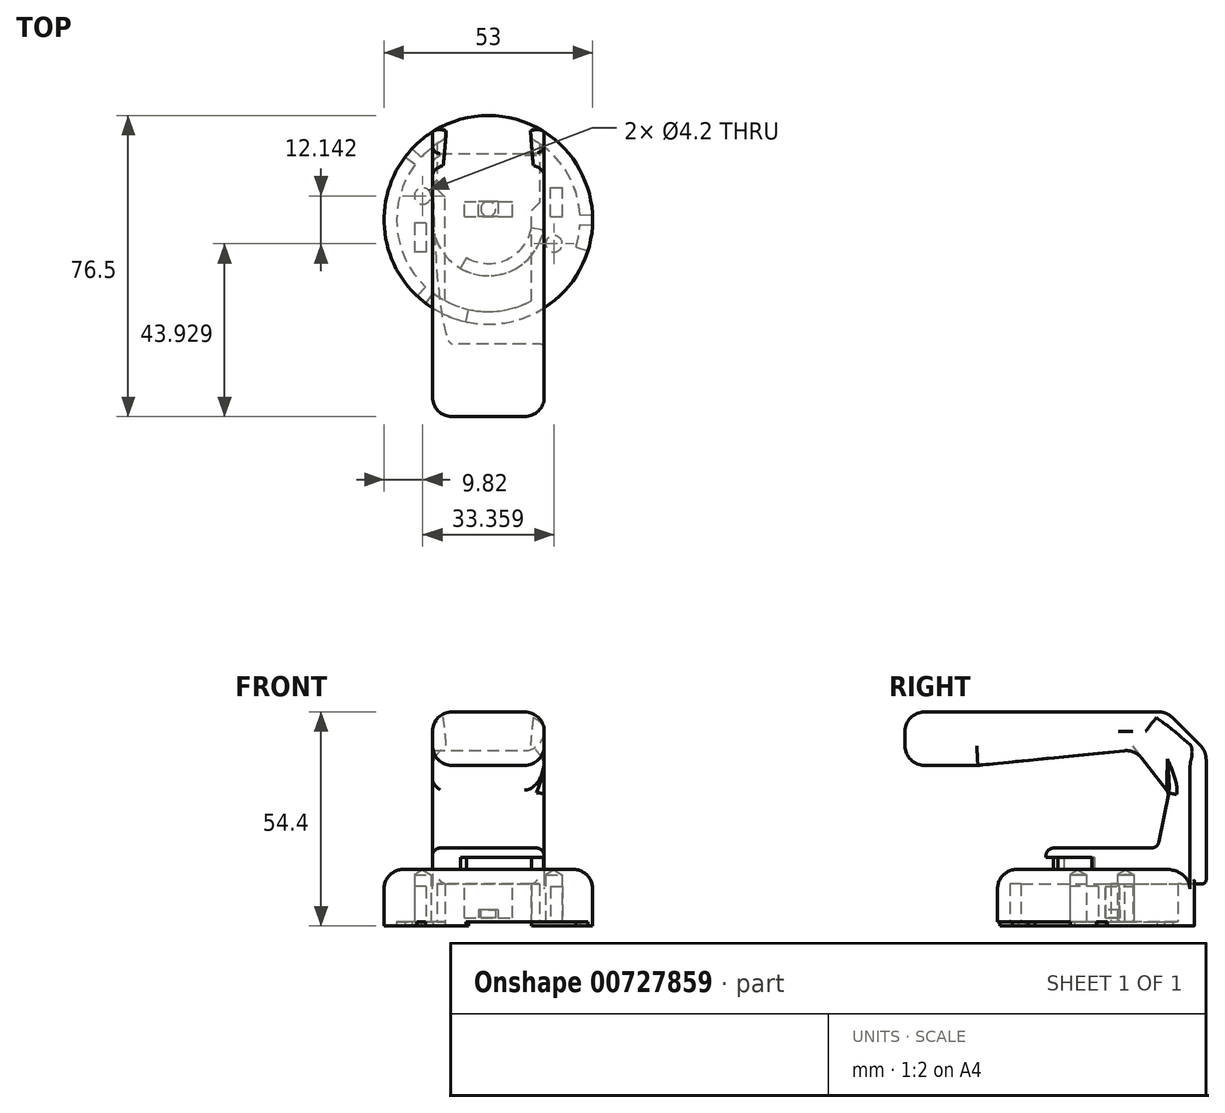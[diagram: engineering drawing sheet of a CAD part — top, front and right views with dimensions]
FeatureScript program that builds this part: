
annotation { "Feature Type Name" : "Feature", "Feature Type Description" : "" }
export const myFeature = defineFeature(function(context is Context, id is Id, definition is map)
    precondition{}
    {
        {
            var Q0;
            Q0=qCreatedBy(makeId("Top.planeOp"),FACE);
            var sketch = newSketch(context, id + "F0", { "sketchPlane" : qUnion([Q0])});
            skCircle(sketch, "E0", {"center": v(0, 0) * mm, "radius": 26.5 * mm});
            skSolve(sketch);
        }
        {
            var Q0;
            Q0=makeQuery(id+"F0.imprint","IMPRINT",FACE,{"disambiguationData":[TD([[makeQuery(id+"F0.imprint","IMPRINT",EDGE,{"derivedFrom":sQuery(id+"F0.wireOp",EDGE,"E0")}),1.0]])]});
            extrude(context, id + "F1", {"entities" : qUnion([Q0]), "depth" : 14.4 * mm, "offsetDistance" : 25 * mm});
        }
        {
            var Q0;
            Q0=makeQuery(id+"F1.opExtrude","CAP_FACE",FACE,{"disambiguationData":[OSD([sQuery(id+"F0.wireOp",EDGE,"E0")])],"isStart":false});
            var sketch = newSketch(context, id + "F2", { "sketchPlane" : qUnion([Q0])});
            skCircle(sketch, "E1", {"center": v(0, 0) * mm, "radius": 14.2 * mm});
            skSolve(sketch);
        }
        {
            var Q0;
            Q0 = qSketchRegion(id + "F2", true);
            extrude(context, id + "F3", {"entities" : qUnion([Q0]), "depth" : 5.4 * mm, "offsetDistance" : 25 * mm});
        }
        {
            var Q0;
            Q0=makeQuery(id+"F1.opExtrude","CAP_FACE",FACE,{"disambiguationData":[OSD([sQuery(id+"F0.wireOp",EDGE,"E0")])],"isStart":false});
            var sketch = newSketch(context, id + "F4", { "sketchPlane" : qUnion([Q0])});
            skLineSegment(sketch, "E2", {"start": v(0, 0) * mm, "end": v(-7.1, -12.3) * mm});
            skLineSegment(sketch, "E3", {"start": v(0, 0) * mm, "end": v(13.98, -2.47) * mm});
            skArc(sketch, "E4", {"start": v(13.98, -2.47) * mm, "mid": v(6, -12.87) * mm, "end": v(-7.1, -12.3) * mm});
            skSolve(sketch);
        }
        {
            var Q0;
            Q0 = qSketchRegion(id + "F4", true);
            extrude(context, id + "F5", {"entities" : qUnion([Q0]), "operationType" : NewBodyOperationType.REMOVE, "depth" : 3 * mm, "offsetDistance" : 25 * mm});
        }
        {
            var Q0;
            Q0=makeQuery(id+"F1.opExtrude","CAP_FACE",FACE,{"disambiguationData":[OSD([sQuery(id+"F0.wireOp",EDGE,"E0")])],"isStart":false});
            var sketch = newSketch(context, id + "F6", { "sketchPlane" : qUnion([Q0])});
            skCircle(sketch, "E5", {"center": v(0, 0) * mm, "radius": 11.1 * mm});
            skSolve(sketch);
        }
        {
            var Q0;
            Q0 = qSketchRegion(id + "F6", true);
            var Q1;
            Q1=makeQuery(id+"F5.boolean.opBoolean","COPY",FACE,{"derivedFrom":makeQuery(id+"F5.opExtrude","CAP_FACE",FACE,{"disambiguationData":[OSD([sQuery(id+"F4.wireOp",EDGE,"E2"),sQuery(id+"F4.wireOp",EDGE,"E3"),sQuery(id+"F4.wireOp",EDGE,"E4")])],"isStart":false})});
            extrude(context, id + "F7", {"entities" : qUnion([Q0]), "endBound" : BoundingType.UP_TO_SURFACE, "depth" : 25 * mm, "endBoundEntityFace" : qUnion([Q1]), "offsetDistance" : 25 * mm});
        }
        {
            var Q0;
            Q0=makeQuery(id+"F1.opExtrude","CAP_FACE",FACE,{"disambiguationData":[OSD([sQuery(id+"F0.wireOp",EDGE,"E0")])],"isStart":true});
            var sketch = newSketch(context, id + "F8", { "sketchPlane" : qUnion([Q0])});
            skCircle(sketch, "E6", {"center": v(0, 0) * mm, "radius": 23.3 * mm});
            skSolve(sketch);
        }
        {
            var Q0;
            Q0 = qSketchRegion(id + "F8", true);
            extrude(context, id + "F9", {"entities" : qUnion([Q0]), "operationType" : NewBodyOperationType.REMOVE, "oppositeDirection" : true, "depth" : 1 * mm, "offsetDistance" : 25 * mm});
        }
        {
            var Q0;
            Q0=makeQuery(id+"F8.imprint","IMPRINT",FACE,{"disambiguationData":[TD([[makeQuery(id+"F8.imprint","IMPRINT",EDGE,{"derivedFrom":sQuery(id+"F8.wireOp",EDGE,"E6")}),-1.0]])]});
            var sketch = newSketch(context, id + "F10", { "sketchPlane" : qUnion([Q0])});
            skLineSegment(sketch, "E7.top", {"start": v(-11, -26.5) * mm, "end": v(11, -26.5) * mm});
            skLineSegment(sketch, "E7.left", {"start": v(-11, 20.54) * mm, "end": v(-11, -26.5) * mm});
            skLineSegment(sketch, "E7.right", {"start": v(11, 20.54) * mm, "end": v(11, -26.5) * mm});
            skArc(sketch, "E8", {"start": v(-11, 20.54) * mm, "mid": v(0, 23.3) * mm, "end": v(11, 20.54) * mm});
            skSolve(sketch);
        }
        {
            var Q0;
            Q0 = qSketchRegion(id + "F10", true);
            extrude(context, id + "F11", {"entities" : qUnion([Q0]), "operationType" : NewBodyOperationType.REMOVE, "oppositeDirection" : true, "depth" : 10.7 * mm, "offsetDistance" : 25 * mm});
        }
        {
            var Q0;
            Q0=makeQuery(id+"F8.imprint","IMPRINT",FACE,{"disambiguationData":[TD([[makeQuery(id+"F8.imprint","IMPRINT",EDGE,{"derivedFrom":sQuery(id+"F8.wireOp",EDGE,"E6")}),-1.0]])]});
            var sketch = newSketch(context, id + "F12", { "sketchPlane" : qUnion([Q0])});
            skLineSegment(sketch, "E9.top", {"start": v(13, -4.34) * mm, "end": v(0, -4.34) * mm});
            skLineSegment(sketch, "E9.left", {"start": v(13, -19.34) * mm, "end": v(13, -4.34) * mm});
            skLineSegment(sketch, "E9.right", {"start": v(0, -23.3) * mm, "end": v(0, -4.34) * mm});
            skArc(sketch, "E10", {"start": v(13, -19.34) * mm, "mid": v(6.8, -22.29) * mm, "end": v(0, -23.3) * mm});
            skSolve(sketch);
        }
        {
            var Q0;
            Q0 = qSketchRegion(id + "F12", true);
            var Q1;
            Q1=makeQuery(id+"F11.boolean.opBoolean","COPY",FACE,{"derivedFrom":makeQuery(id+"F11.opExtrude","CAP_FACE",FACE,{"disambiguationData":[OSD([sQuery(id+"F10.wireOp",EDGE,"E7.top"),sQuery(id+"F10.wireOp",EDGE,"E7.left"),sQuery(id+"F10.wireOp",EDGE,"E7.right"),sQuery(id+"F10.wireOp",EDGE,"E8")])],"isStart":false})});
            extrude(context, id + "F13", {"entities" : qUnion([Q0]), "operationType" : NewBodyOperationType.REMOVE, "endBound" : BoundingType.UP_TO_SURFACE, "oppositeDirection" : true, "depth" : 10.7 * mm, "endBoundEntityFace" : qUnion([Q1]), "offsetDistance" : 25 * mm});
        }
        {
            var Q0;
            Q0=makeQuery(id+"F13.boolean.opBoolean","INTERSECT",EDGE,{"derivedFrom":[makeQuery(id+"F11.boolean.opBoolean","COPY",FACE,{"derivedFrom":makeQuery(id+"F11.opExtrude","SWEPT_FACE",FACE,{"disambiguationData":[OSD([sQuery(id+"F10.wireOp",EDGE,"E7.right")])]})}),makeQuery(id+"F13.opExtrude","SWEPT_FACE",FACE,{"disambiguationData":[OSD([sQuery(id+"F12.wireOp",EDGE,"E9.top")])]})]});
            chamfer(context, id + "F14", {"entities" : qUnion([Q0]), "width" : 2 * mm, "tangentPropagation" : true});
        }
        {
            var Q0;
            Q0=makeQuery(id+"F8.imprint","IMPRINT",FACE,{"disambiguationData":[TD([[makeQuery(id+"F8.imprint","IMPRINT",EDGE,{"derivedFrom":sQuery(id+"F8.wireOp",EDGE,"E6")}),-1.0]])]});
            var sketch = newSketch(context, id + "F15", { "sketchPlane" : qUnion([Q0])});
            skLineSegment(sketch, "E11.top", {"start": v(-13, -7.84) * mm, "end": v(0, -7.84) * mm});
            skLineSegment(sketch, "E11.left", {"start": v(-13, -19.34) * mm, "end": v(-13, -7.84) * mm});
            skLineSegment(sketch, "E11.right", {"start": v(0, -23.3) * mm, "end": v(0, -7.84) * mm});
            skArc(sketch, "E12", {"start": v(-13, -19.34) * mm, "mid": v(-6.8, -22.29) * mm, "end": v(0, -23.3) * mm});
            skSolve(sketch);
        }
        {
            var Q0;
            Q0 = qSketchRegion(id + "F15", true);
            var Q1;
            Q1=makeQuery(id+"F13.boolean.opBoolean","MERGE",FACE,{"derivedFrom":[makeQuery(id+"F11.boolean.opBoolean","COPY",FACE,{"derivedFrom":makeQuery(id+"F11.opExtrude","CAP_FACE",FACE,{"disambiguationData":[OSD([sQuery(id+"F10.wireOp",EDGE,"E7.top"),sQuery(id+"F10.wireOp",EDGE,"E7.left"),sQuery(id+"F10.wireOp",EDGE,"E7.right"),sQuery(id+"F10.wireOp",EDGE,"E8")])],"isStart":false})})],"fromTools":[makeQuery(id+"F13.opExtrude","CAP_FACE",FACE,{"disambiguationData":[OSD([sQuery(id+"F12.wireOp",EDGE,"E9.top"),sQuery(id+"F12.wireOp",EDGE,"E9.left"),sQuery(id+"F12.wireOp",EDGE,"E9.right"),sQuery(id+"F12.wireOp",EDGE,"E10")])],"isStart":false})]});
            extrude(context, id + "F16", {"entities" : qUnion([Q0]), "operationType" : NewBodyOperationType.REMOVE, "endBound" : BoundingType.UP_TO_SURFACE, "oppositeDirection" : true, "depth" : 25 * mm, "endBoundEntityFace" : qUnion([Q1]), "offsetDistance" : 25 * mm});
        }
        {
            var Q0;
            Q0=makeQuery(id+"F16.boolean.opBoolean","INTERSECT",EDGE,{"derivedFrom":[makeQuery(id+"F11.boolean.opBoolean","COPY",FACE,{"derivedFrom":makeQuery(id+"F11.opExtrude","SWEPT_FACE",FACE,{"disambiguationData":[OSD([sQuery(id+"F10.wireOp",EDGE,"E7.left")])]})}),makeQuery(id+"F16.opExtrude","SWEPT_FACE",FACE,{"disambiguationData":[OSD([sQuery(id+"F15.wireOp",EDGE,"E11.top")])]})]});
            chamfer(context, id + "F17", {"entities" : qUnion([Q0]), "width" : 2 * mm, "tangentPropagation" : true});
        }
        {
            var Q0;
            Q0=makeQuery(id+"F16.boolean.opBoolean","MERGE",FACE,{"derivedFrom":[makeQuery(id+"F13.boolean.opBoolean","MERGE",FACE,{"derivedFrom":[makeQuery(id+"F11.boolean.opBoolean","COPY",FACE,{"derivedFrom":makeQuery(id+"F11.opExtrude","CAP_FACE",FACE,{"disambiguationData":[OSD([sQuery(id+"F10.wireOp",EDGE,"E7.top"),sQuery(id+"F10.wireOp",EDGE,"E7.left"),sQuery(id+"F10.wireOp",EDGE,"E7.right"),sQuery(id+"F10.wireOp",EDGE,"E8")])],"isStart":false})})],"fromTools":[makeQuery(id+"F13.opExtrude","CAP_FACE",FACE,{"disambiguationData":[OSD([sQuery(id+"F12.wireOp",EDGE,"E9.top"),sQuery(id+"F12.wireOp",EDGE,"E9.left"),sQuery(id+"F12.wireOp",EDGE,"E9.right"),sQuery(id+"F12.wireOp",EDGE,"E10")])],"isStart":false})]})],"fromTools":[makeQuery(id+"F16.opExtrude","CAP_FACE",FACE,{"disambiguationData":[OSD([sQuery(id+"F15.wireOp",EDGE,"E11.top"),sQuery(id+"F15.wireOp",EDGE,"E11.left"),sQuery(id+"F15.wireOp",EDGE,"E11.right"),sQuery(id+"F15.wireOp",EDGE,"E12")])],"isStart":false})]});
            var sketch = newSketch(context, id + "F18", { "sketchPlane" : qUnion([Q0])});
            skLineSegment(sketch, "E13.bottom", {"start": v(-6.1, -4.65) * mm, "end": v(6.1, -4.65) * mm});
            skLineSegment(sketch, "E13.top", {"start": v(-6.1, -0.85) * mm, "end": v(6.1, -0.85) * mm});
            skLineSegment(sketch, "E13.left", {"start": v(-6.1, -0.85) * mm, "end": v(-6.1, -4.65) * mm});
            skLineSegment(sketch, "E13.right", {"start": v(6.1, -0.85) * mm, "end": v(6.1, -4.65) * mm});
            skSolve(sketch);
        }
        {
            var Q0;
            Q0 = qSketchRegion(id + "F18", true);
            extrude(context, id + "F19", {"entities" : qUnion([Q0]), "operationType" : NewBodyOperationType.ADD, "depth" : 8.65 * mm, "offsetDistance" : 25 * mm});
        }
        {
            var Q0;
            Q0=makeQuery(id+"F8.imprint","IMPRINT",FACE,{"disambiguationData":[TD([[makeQuery(id+"F8.imprint","IMPRINT",EDGE,{"derivedFrom":sQuery(id+"F8.wireOp",EDGE,"E6")}),1.0]])]});
            var sketch = newSketch(context, id + "F20", { "sketchPlane" : qUnion([Q0])});
            skLineSegment(sketch, "E14.bottom", {"start": v(-2.5, -0.85) * mm, "end": v(2.5, -0.85) * mm});
            skLineSegment(sketch, "E14.top", {"start": v(-2.5, -4.65) * mm, "end": v(2.5, -4.65) * mm});
            skLineSegment(sketch, "E14.left", {"start": v(-2.5, -0.85) * mm, "end": v(-2.5, -4.65) * mm});
            skLineSegment(sketch, "E14.right", {"start": v(2.5, -0.85) * mm, "end": v(2.5, -4.65) * mm});
            skSolve(sketch);
        }
        {
            var Q0;
            Q0 = qSketchRegion(id + "F20", true);
            var Q1;
            Q1=makeQuery(id+"F19.opExtrude","CAP_FACE",FACE,{"disambiguationData":[OSD([sQuery(id+"F18.wireOp",EDGE,"E13.bottom"),sQuery(id+"F18.wireOp",EDGE,"E13.top"),sQuery(id+"F18.wireOp",EDGE,"E13.left"),sQuery(id+"F18.wireOp",EDGE,"E13.right")])],"isStart":false});
            extrude(context, id + "F21", {"entities" : qUnion([Q0]), "operationType" : NewBodyOperationType.REMOVE, "endBound" : BoundingType.UP_TO_SURFACE, "oppositeDirection" : true, "depth" : 25 * mm, "endBoundEntityFace" : qUnion([Q1]), "hasOffset" : true, "offsetDistance" : 2 * mm, "offsetOppositeDirection" : true});
        }
        {
            var Q0;
            Q0=makeQuery(id+"F21.boolean.opBoolean","COPY",FACE,{"derivedFrom":makeQuery(id+"F21.opExtrude","CAP_FACE",FACE,{"disambiguationData":[OSD([sQuery(id+"F20.wireOp",EDGE,"E14.bottom"),sQuery(id+"F20.wireOp",EDGE,"E14.top"),sQuery(id+"F20.wireOp",EDGE,"E14.left"),sQuery(id+"F20.wireOp",EDGE,"E14.right")])],"isStart":false})});
            var sketch = newSketch(context, id + "F22", { "sketchPlane" : qUnion([Q0])});
            skCircle(sketch, "E15", {"center": v(0, -2.75) * mm, "radius": 1.9 * mm});
            skLineSegment(sketch, "E16", {"start": v(-2.5, -0.85) * mm, "end": v(2.5, -4.65) * mm, "construction": true});
            skLineSegment(sketch, "E17", {"start": v(2.5, -0.85) * mm, "end": v(-2.5, -4.65) * mm, "construction": true});
            skSolve(sketch);
        }
        {
            var Q0;
            Q0 = qSketchRegion(id + "F22", true);
            var Q1;
            {var subQ0=sQuery(id+"F18.wireOp",EDGE,"E13.bottom");var subQ1=sQuery(id+"F18.wireOp",EDGE,"E13.top");var subQ2=sQuery(id+"F18.wireOp",EDGE,"E13.left");Q1=makeQuery(id+"F21.boolean.opBoolean","SPLIT",FACE,{"disambiguationData":[TD([makeQuery(id+"F19.opExtrude","SWEPT_FACE",FACE,{"disambiguationData":[OSD([subQ2])]})])],"derivedFrom":makeQuery(id+"F19.opExtrude","CAP_FACE",FACE,{"disambiguationData":[OSD([subQ0,subQ1,subQ2,sQuery(id+"F18.wireOp",EDGE,"E13.right")])],"isStart":false})});}
            extrude(context, id + "F23", {"entities" : qUnion([Q0]), "operationType" : NewBodyOperationType.ADD, "endBound" : BoundingType.UP_TO_SURFACE, "depth" : 25 * mm, "endBoundEntityFace" : qUnion([Q1]), "offsetDistance" : 25 * mm});
        }
        {
            var Q0;
            Q0=makeQuery(id+"F8.imprint","IMPRINT",FACE,{"disambiguationData":[TD([[makeQuery(id+"F8.imprint","IMPRINT",EDGE,{"derivedFrom":sQuery(id+"F8.wireOp",EDGE,"E6")}),1.0]])]});
            var sketch = newSketch(context, id + "F24", { "sketchPlane" : qUnion([Q0])});
            skPoint(sketch, "E18", {"position": v(16.68, 6.07) * mm});
            skPoint(sketch, "E19", {"position": v(-16.68, -6.07) * mm});
            skLineSegment(sketch, "E20", {"start": v(-16.68, -6.07) * mm, "end": v(16.68, 6.07) * mm, "construction": true});
            skLineSegment(sketch, "E21", {"start": v(-16.68, -6.07) * mm, "end": v(16.68, -6.07) * mm, "construction": true});
            skCircle(sketch, "E22", {"center": v(0, 0) * mm, "radius": 17.75 * mm, "construction": true});
            skSolve(sketch);
        }
        {
            var Q0;
            Q0=sQuery(id+"F24.wireOp",VERTEX,"E18");
            var Q1;
            Q1=sQuery(id+"F24.wireOp",VERTEX,"E19");
            var Q2;
            Q2=makeQuery(id+"F1.opExtrude","SWEPT_BODY",BODY,{"disambiguationData":[OSD([sQuery(id+"F0.wireOp",EDGE,"E0")])]});
            hole(context, id + "F25", {"style" : HoleStyle.SIMPLE, "endStyle" : HoleEndStyle.BLIND, "standardTappedOrClearance" : lookupTablePath({ "standard" : "ISO", "engagement" : "75%", "pitch" : "0.8 mm", "size" : "M5", "type" : "Tapped" }), "standardBlindInLast" : lookupTablePath({ "standard" : "ISO", "engagement" : "75%", "pitch" : "0.8 mm", "size" : "M5", "type" : "Tapped" }), "holeDiameter" : 4.2 * mm, "majorDiameter" : 5 * mm, "showTappedDepth" : true, "holeDepth" : 12 * mm, "isTappedThrough" : true, "tappedDepth" : 9.6 * mm, "tapClearance" : 3, "locations" : qUnion([Q0, Q1]), "scope" : qUnion([Q2])});
        }
        {
            var Q0;
            Q0=makeQuery(id+"F1.opExtrude","CAP_FACE",FACE,{"disambiguationData":[OSD([sQuery(id+"F0.wireOp",EDGE,"E0")])],"isStart":false});
            var sketch = newSketch(context, id + "F26", { "sketchPlane" : qUnion([Q0])});
            skLineSegment(sketch, "E23.bottom", {"start": v(14.2, 0) * mm, "end": v(-14.2, 0) * mm});
            skLineSegment(sketch, "E23.left", {"start": v(14.2, 0) * mm, "end": v(14.2, 22.37) * mm});
            skLineSegment(sketch, "E23.right", {"start": v(-14.2, 0) * mm, "end": v(-14.2, 22.37) * mm});
            skArc(sketch, "E24", {"start": v(14.2, 22.37) * mm, "mid": v(0, 26.5) * mm, "end": v(-14.2, 22.37) * mm});
            skSolve(sketch);
        }
        {
            var Q0;
            Q0 = qSketchRegion(id + "F26", true);
            extrude(context, id + "F27", {"entities" : qUnion([Q0]), "depth" : 40 * mm, "offsetDistance" : 25 * mm});
        }
        {
            var Q0;
            Q0=makeQuery(id+"F27.opExtrude","SWEPT_FACE",FACE,{"disambiguationData":[OSD([sQuery(id+"F26.wireOp",EDGE,"E23.bottom")])]});
            var sketch = newSketch(context, id + "F28", { "sketchPlane" : qUnion([Q0])});
            skLineSegment(sketch, "E25.bottom", {"start": v(-14.2, 54.4) * mm, "end": v(14.2, 54.4) * mm});
            skLineSegment(sketch, "E25.top", {"start": v(-14.2, 40.8) * mm, "end": v(14.2, 40.8) * mm});
            skLineSegment(sketch, "E25.left", {"start": v(-14.2, 54.4) * mm, "end": v(-14.2, 40.8) * mm});
            skLineSegment(sketch, "E25.right", {"start": v(14.2, 54.4) * mm, "end": v(14.2, 40.8) * mm});
            skSolve(sketch);
        }
        {
            var Q0;
            Q0 = qSketchRegion(id + "F28", true);
            extrude(context, id + "F29", {"entities" : qUnion([Q0]), "operationType" : NewBodyOperationType.ADD, "depth" : 50 * mm, "offsetDistance" : 25 * mm});
        }
        {
            var Q0;
            Q0=makeQuery(id+"F27.opExtrude","CAP_EDGE",EDGE,{"disambiguationData":[OSD([sQuery(id+"F26.wireOp",EDGE,"E24")])],"isStart":false});
            chamfer(context, id + "F30", {"entities" : qUnion([Q0]), "width" : 10 * mm, "tangentPropagation" : true});
        }
        {
            var Q0;
            Q0=makeQuery(id+"F29.boolean.opBoolean","MERGE",FACE,{"derivedFrom":[makeQuery(id+"F27.opExtrude","SWEPT_FACE",FACE,{"disambiguationData":[OSD([sQuery(id+"F26.wireOp",EDGE,"E23.right")])]}),makeQuery(id+"F29.opExtrude","SWEPT_FACE",FACE,{"disambiguationData":[OSD([sQuery(id+"F28.wireOp",EDGE,"E25.left")])]})]});
            var sketch = newSketch(context, id + "F31", { "sketchPlane" : qUnion([Q0])});
            skLineSegment(sketch, "E26", {"start": v(31.5, 40.8) * mm, "end": v(-8.5, 44.8) * mm});
            skLineSegment(sketch, "E27", {"start": v(-8.5, 44.8) * mm, "end": v(-17, 33.8) * mm});
            skLineSegment(sketch, "E28", {"start": v(-17, 33.8) * mm, "end": v(-14.2, 19.8) * mm});
            skLineSegment(sketch, "E29", {"start": v(-14.2, 19.8) * mm, "end": v(0, 19.8) * mm});
            skLineSegment(sketch, "E30", {"start": v(0, 19.8) * mm, "end": v(0, 40.8) * mm});
            skLineSegment(sketch, "E31", {"start": v(0, 40.8) * mm, "end": v(31.5, 40.8) * mm});
            skSolve(sketch);
        }
        {
            var Q0;
            Q0 = qSketchRegion(id + "F31", true);
            extrude(context, id + "F32", {"entities" : qUnion([Q0]), "operationType" : NewBodyOperationType.REMOVE, "endBound" : BoundingType.THROUGH_ALL, "oppositeDirection" : true, "depth" : 25 * mm, "offsetDistance" : 25 * mm});
        }
        {
            var Q0;
            Q0=makeQuery(id+"F27.opExtrude","SWEPT_BODY",BODY,{"disambiguationData":[OSD([sQuery(id+"F26.wireOp",EDGE,"E23.bottom"),sQuery(id+"F26.wireOp",EDGE,"E23.left"),sQuery(id+"F26.wireOp",EDGE,"E23.right"),sQuery(id+"F26.wireOp",EDGE,"E24")])]});
            var Q1;
            Q1=makeQuery(id+"F1.opExtrude","SWEPT_BODY",BODY,{"disambiguationData":[OSD([sQuery(id+"F0.wireOp",EDGE,"E0")])]});
            var Q2;
            Q2=makeQuery(id+"F3.opExtrude","SWEPT_BODY",BODY,{"disambiguationData":[OSD([sQuery(id+"F2.wireOp",EDGE,"E1")])]});
            var Q3;
            Q3=makeQuery(id+"F7.opExtrude","SWEPT_BODY",BODY,{"disambiguationData":[OSD([sQuery(id+"F6.wireOp",EDGE,"E5")])]});
            booleanBodies(context, id + "F33", {"operationType" : BooleanOperationType.UNION, "tools" : qUnion([Q0, Q1, Q2, Q3])});
        }
        {
            var Q0;
            Q0=makeQuery(id+"F27.opExtrude","CAP_EDGE",EDGE,{"disambiguationData":[OSD([sQuery(id+"F26.wireOp",EDGE,"E23.right")])],"isStart":true});
            var Q1;
            {var subQ0=sQuery(id+"F2.wireOp",EDGE,"E1");Q1=makeQuery(id+"F33.opBoolean","SPLIT",EDGE,{"disambiguationData":[TD([makeQuery(id+"F5.boolean.opBoolean","COPY",FACE,{"derivedFrom":makeQuery(id+"F5.opExtrude","SWEPT_FACE",FACE,{"disambiguationData":[OSD([sQuery(id+"F4.wireOp",EDGE,"E2")])]})})])],"derivedFrom":makeQuery(id+"F3.opExtrude","CAP_EDGE",EDGE,{"disambiguationData":[OSD([subQ0])],"isStart":true})});}
            var Q2;
            Q2=makeQuery(id+"F33.opBoolean","MERGE",FACE,{"derivedFrom":[makeQuery(id+"F3.opExtrude","CAP_FACE",FACE,{"disambiguationData":[OSD([sQuery(id+"F2.wireOp",EDGE,"E1")])],"isStart":false}),makeQuery(id+"F32.boolean.opBoolean","COPY",FACE,{"derivedFrom":makeQuery(id+"F32.opExtrude","SWEPT_FACE",FACE,{"disambiguationData":[OSD([sQuery(id+"F31.wireOp",EDGE,"E29")])]})})]});
            var Q3;
            Q3=makeQuery(id+"F27.opExtrude","CAP_EDGE",EDGE,{"disambiguationData":[OSD([sQuery(id+"F26.wireOp",EDGE,"E23.left")])],"isStart":true});
            var Q4;
            {var subQ0=sQuery(id+"F2.wireOp",EDGE,"E1");Q4=makeQuery(id+"F33.opBoolean","SPLIT",EDGE,{"disambiguationData":[TD([makeQuery(id+"F5.boolean.opBoolean","COPY",FACE,{"derivedFrom":makeQuery(id+"F5.opExtrude","SWEPT_FACE",FACE,{"disambiguationData":[OSD([sQuery(id+"F4.wireOp",EDGE,"E3")])]})})])],"derivedFrom":makeQuery(id+"F3.opExtrude","CAP_EDGE",EDGE,{"disambiguationData":[OSD([subQ0])],"isStart":true})});}
            fillet(context, id + "F34", {"entities" : qUnion([Q0, Q1, Q2, Q3, Q4]), "radius" : 2 * mm, "allowEdgeOverflow" : false});
        }
        {
            var Q0;
            Q0=makeQuery(id+"F29.boolean.opBoolean","MERGE",FACE,{"derivedFrom":[makeQuery(id+"F27.opExtrude","CAP_FACE",FACE,{"disambiguationData":[OSD([sQuery(id+"F26.wireOp",EDGE,"E23.bottom"),sQuery(id+"F26.wireOp",EDGE,"E23.left"),sQuery(id+"F26.wireOp",EDGE,"E23.right"),sQuery(id+"F26.wireOp",EDGE,"E24")])],"isStart":false}),makeQuery(id+"F29.opExtrude","SWEPT_FACE",FACE,{"disambiguationData":[OSD([sQuery(id+"F28.wireOp",EDGE,"E25.bottom")])]})]});
            var Q1;
            Q1=makeQuery(id+"F29.opExtrude","CAP_FACE",FACE,{"disambiguationData":[OSD([sQuery(id+"F28.wireOp",EDGE,"E25.bottom"),sQuery(id+"F28.wireOp",EDGE,"E25.top"),sQuery(id+"F28.wireOp",EDGE,"E25.left"),sQuery(id+"F28.wireOp",EDGE,"E25.right")])],"isStart":false});
            var Q2;
            Q2=makeQuery(id+"F29.opExtrude","SWEPT_EDGE",EDGE,{"disambiguationData":[OSD([sQuery(id+"F26.wireOp",EDGE,"E23.bottom"),sQuery(id+"F26.wireOp",EDGE,"E23.right"),sQuery(id+"F28.wireOp",EDGE,"E25.top"),sQuery(id+"F28.wireOp",EDGE,"E25.left")])]});
            var Q3;
            Q3=makeQuery(id+"F32.boolean.opBoolean","COPY",EDGE,{"derivedFrom":makeQuery(id+"F32.opExtrude","CAP_EDGE",EDGE,{"disambiguationData":[OSD([sQuery(id+"F31.wireOp",EDGE,"E26")])],"isStart":true})});
            var Q4;
            Q4=makeQuery(id+"F32.boolean.opBoolean","COPY",EDGE,{"derivedFrom":makeQuery(id+"F32.opExtrude","CAP_EDGE",EDGE,{"disambiguationData":[OSD([sQuery(id+"F31.wireOp",EDGE,"E27")])],"isStart":true})});
            var Q5;
            Q5=makeQuery(id+"F29.opExtrude","SWEPT_EDGE",EDGE,{"disambiguationData":[OSD([sQuery(id+"F26.wireOp",EDGE,"E23.bottom"),sQuery(id+"F26.wireOp",EDGE,"E23.left"),sQuery(id+"F28.wireOp",EDGE,"E25.top"),sQuery(id+"F28.wireOp",EDGE,"E25.right")])]});
            var Q6;
            Q6=makeQuery(id+"F32.boolean.opBoolean","INTERSECT",EDGE,{"derivedFrom":[makeQuery(id+"F29.boolean.opBoolean","MERGE",FACE,{"derivedFrom":[makeQuery(id+"F27.opExtrude","SWEPT_FACE",FACE,{"disambiguationData":[OSD([sQuery(id+"F26.wireOp",EDGE,"E23.left")])]}),makeQuery(id+"F29.opExtrude","SWEPT_FACE",FACE,{"disambiguationData":[OSD([sQuery(id+"F28.wireOp",EDGE,"E25.right")])]})]}),makeQuery(id+"F32.opExtrude","SWEPT_FACE",FACE,{"disambiguationData":[OSD([sQuery(id+"F31.wireOp",EDGE,"E26")])]})]});
            var Q7;
            Q7=makeQuery(id+"F32.boolean.opBoolean","INTERSECT",EDGE,{"derivedFrom":[makeQuery(id+"F29.boolean.opBoolean","MERGE",FACE,{"derivedFrom":[makeQuery(id+"F27.opExtrude","SWEPT_FACE",FACE,{"disambiguationData":[OSD([sQuery(id+"F26.wireOp",EDGE,"E23.left")])]}),makeQuery(id+"F29.opExtrude","SWEPT_FACE",FACE,{"disambiguationData":[OSD([sQuery(id+"F28.wireOp",EDGE,"E25.right")])]})]}),makeQuery(id+"F32.opExtrude","SWEPT_FACE",FACE,{"disambiguationData":[OSD([sQuery(id+"F31.wireOp",EDGE,"E27")])]})]});
            var Q8;
            Q8=makeQuery(id+"F1.opExtrude","CAP_EDGE",EDGE,{"disambiguationData":[OSD([sQuery(id+"F0.wireOp",EDGE,"E0")])],"isStart":false});
            var Q9;
            Q9=makeQuery(id+"F32.boolean.opBoolean","COPY",EDGE,{"derivedFrom":makeQuery(id+"F32.opExtrude","SWEPT_EDGE",EDGE,{"disambiguationData":[OSD([sQuery(id+"F31.wireOp",EDGE,"E26"),sQuery(id+"F31.wireOp",EDGE,"E27")])]})});
            fillet(context, id + "F35", {"entities" : qUnion([Q0, Q1, Q2, Q3, Q4, Q5, Q6, Q7, Q8, Q9]), "radius" : 5 * mm, "tangentPropagation" : true, "allowEdgeOverflow" : false});
        }
        {
            var Q0;
            Q0=makeQuery(id+"F30.opChamfer","BLEND_FACE",FACE,{"disambiguationData":[OSD([sQuery(id+"F26.wireOp",EDGE,"E24")])]});
            fillet(context, id + "F36", {"entities" : qUnion([Q0]), "radius" : 5 * mm, "tangentPropagation" : true, "allowEdgeOverflow" : false});
        }
        {
            var Q0;
            Q0=makeQuery(id+"F32.boolean.opBoolean","COPY",FACE,{"derivedFrom":makeQuery(id+"F32.opExtrude","SWEPT_FACE",FACE,{"disambiguationData":[OSD([sQuery(id+"F31.wireOp",EDGE,"E28")])]})});
            fillet(context, id + "F37", {"entities" : qUnion([Q0]), "radius" : 2 * mm, "tangentPropagation" : true, "allowEdgeOverflow" : false});
        }
        {
            var Q0;
            Q0=makeQuery(id+"F8.imprint","IMPRINT",FACE,{"disambiguationData":[TD([[makeQuery(id+"F8.imprint","IMPRINT",EDGE,{"derivedFrom":sQuery(id+"F8.wireOp",EDGE,"E6")}),-1.0]])]});
            var sketch = newSketch(context, id + "F38", { "sketchPlane" : qUnion([Q0])});
            skLineSegment(sketch, "E32", {"start": v(-5.69, 25.88) * mm, "end": v(0, 0) * mm});
            skLineSegment(sketch, "E33", {"start": v(0, 0) * mm, "end": v(25.29, 7.92) * mm});
            skArc(sketch, "E34", {"start": v(-5.69, 25.88) * mm, "mid": v(13.3, 22.92) * mm, "end": v(25.29, 7.92) * mm});
            skLineSegment(sketch, "E35", {"start": v(-5, 22.76) * mm, "end": v(0, 22.76) * mm, "construction": true});
            skSolve(sketch);
        }
        {
            var Q0;
            Q0 = qSketchRegion(id + "F38", true);
            extrude(context, id + "F39", {"entities" : qUnion([Q0]), "operationType" : NewBodyOperationType.REMOVE, "oppositeDirection" : true, "depth" : 1 * mm, "offsetDistance" : 25 * mm});
        }
        {
            var Q0;
            Q0=makeQuery(id+"F8.imprint","IMPRINT",FACE,{"disambiguationData":[TD([[makeQuery(id+"F8.imprint","IMPRINT",EDGE,{"derivedFrom":sQuery(id+"F8.wireOp",EDGE,"E6")}),-1.0]])]});
            var sketch = newSketch(context, id + "F40", { "sketchPlane" : qUnion([Q0])});
            skLineSegment(sketch, "E36", {"start": v(0, 0) * mm, "end": v(26.5, 0) * mm, "construction": true});
            skLineSegment(sketch, "E37", {"start": v(0, 0) * mm, "end": v(-17.03, 20.3) * mm, "construction": true});
            skLineSegment(sketch, "E38", {"start": v(0, 0) * mm, "end": v(-20.3, -17.03) * mm, "construction": true});
            skLineSegment(sketch, "E39", {"start": v(0, 0) * mm, "end": v(-15.95, 21.16) * mm, "construction": true});
            skLineSegment(sketch, "E40", {"start": v(0, 0) * mm, "end": v(-18.07, 19.38) * mm, "construction": true});
            skLineSegment(sketch, "E41", {"start": v(26.46, 1.39) * mm, "end": v(0, 0) * mm, "construction": true});
            skLineSegment(sketch, "E42", {"start": v(0, 0) * mm, "end": v(26.46, -1.39) * mm, "construction": true});
            skLineSegment(sketch, "E43", {"start": v(-19.38, -18.07) * mm, "end": v(0, 0) * mm, "construction": true});
            skLineSegment(sketch, "E44", {"start": v(-21.16, -15.95) * mm, "end": v(0, 0) * mm, "construction": true});
            skArc(sketch, "E45", {"start": v(-19.38, -18.07) * mm, "mid": v(-20.3, -17.03) * mm, "end": v(-21.16, -15.95) * mm});
            skArc(sketch, "E46", {"start": v(-18.07, 19.38) * mm, "mid": v(-17.03, 20.3) * mm, "end": v(-15.95, 21.16) * mm});
            skArc(sketch, "E47", {"start": v(26.46, 1.39) * mm, "mid": v(26.5, 0) * mm, "end": v(26.46, -1.39) * mm});
            skArc(sketch, "E48", {"start": v(23.27, -1.22) * mm, "mid": v(23.3, 0) * mm, "end": v(23.27, 1.22) * mm});
            skLineSegment(sketch, "E49", {"start": v(23.27, 1.22) * mm, "end": v(26.46, 1.39) * mm});
            skLineSegment(sketch, "E50", {"start": v(23.27, -1.22) * mm, "end": v(26.46, -1.39) * mm});
            skLineSegment(sketch, "E51", {"start": v(-15.9, 17.04) * mm, "end": v(-18.07, 19.38) * mm});
            skLineSegment(sketch, "E52", {"start": v(-14.02, 18.6) * mm, "end": v(-15.95, 21.16) * mm});
            skLineSegment(sketch, "E53", {"start": v(-17.04, -15.9) * mm, "end": v(-19.38, -18.07) * mm});
            skLineSegment(sketch, "E54", {"start": v(-18.6, -14.02) * mm, "end": v(-21.16, -15.95) * mm});
            skArc(sketch, "E55", {"start": v(-17.04, -15.9) * mm, "mid": v(-17.85, -14.98) * mm, "end": v(-18.6, -14.02) * mm});
            skArc(sketch, "E56", {"start": v(-15.9, 17.04) * mm, "mid": v(-14.98, 17.85) * mm, "end": v(-14.02, 18.6) * mm});
            skSolve(sketch);
        }
        {
            var Q0;
            Q0 = qSketchRegion(id + "F40", true);
            extrude(context, id + "F41", {"entities" : qUnion([Q0]), "operationType" : NewBodyOperationType.REMOVE, "oppositeDirection" : true, "depth" : 1 * mm, "offsetDistance" : 25 * mm});
        }
        {
            var Q0;
            Q0=makeQuery(id+"F11.boolean.opBoolean","INTERSECT",EDGE,{"derivedFrom":[makeQuery(id+"F1.opExtrude","SWEPT_FACE",FACE,{"disambiguationData":[OSD([sQuery(id+"F0.wireOp",EDGE,"E0")])]}),makeQuery(id+"F11.opExtrude","SWEPT_FACE",FACE,{"disambiguationData":[OSD([sQuery(id+"F10.wireOp",EDGE,"E7.left")])]})]});
            var Q1;
            Q1=makeQuery(id+"F11.boolean.opBoolean","INTERSECT",EDGE,{"derivedFrom":[makeQuery(id+"F1.opExtrude","SWEPT_FACE",FACE,{"disambiguationData":[OSD([sQuery(id+"F0.wireOp",EDGE,"E0")])]}),makeQuery(id+"F11.opExtrude","CAP_FACE",FACE,{"disambiguationData":[OSD([sQuery(id+"F10.wireOp",EDGE,"E7.top"),sQuery(id+"F10.wireOp",EDGE,"E7.left"),sQuery(id+"F10.wireOp",EDGE,"E7.right"),sQuery(id+"F10.wireOp",EDGE,"E8")])],"isStart":false})]});
            var Q2;
            Q2=makeQuery(id+"F11.boolean.opBoolean","INTERSECT",EDGE,{"derivedFrom":[makeQuery(id+"F1.opExtrude","SWEPT_FACE",FACE,{"disambiguationData":[OSD([sQuery(id+"F0.wireOp",EDGE,"E0")])]}),makeQuery(id+"F11.opExtrude","SWEPT_FACE",FACE,{"disambiguationData":[OSD([sQuery(id+"F10.wireOp",EDGE,"E7.right")])]})]});
            var Q3;
            Q3=makeQuery(id+"F16.boolean.opBoolean","INTERSECT",EDGE,{"derivedFrom":[makeQuery(id+"F11.boolean.opBoolean","COPY",FACE,{"derivedFrom":makeQuery(id+"F11.opExtrude","SWEPT_FACE",FACE,{"disambiguationData":[OSD([sQuery(id+"F10.wireOp",EDGE,"E7.left")])]})}),makeQuery(id+"F16.opExtrude","SWEPT_FACE",FACE,{"disambiguationData":[OSD([sQuery(id+"F15.wireOp",EDGE,"E12")])]})]});
            var Q4;
            Q4=makeQuery(id+"F13.boolean.opBoolean","INTERSECT",EDGE,{"derivedFrom":[makeQuery(id+"F11.boolean.opBoolean","COPY",FACE,{"derivedFrom":makeQuery(id+"F11.opExtrude","SWEPT_FACE",FACE,{"disambiguationData":[OSD([sQuery(id+"F10.wireOp",EDGE,"E7.right")])]})}),makeQuery(id+"F13.opExtrude","SWEPT_FACE",FACE,{"disambiguationData":[OSD([sQuery(id+"F12.wireOp",EDGE,"E10")])]})]});
            fillet(context, id + "F42", {"entities" : qUnion([Q0, Q1, Q2, Q3, Q4]), "radius" : 1 * mm, "tangentPropagation" : true, "allowEdgeOverflow" : false});
        }
        {
            var Q0;
            {var subQ0=sQuery(id+"F8.wireOp",EDGE,"E6");Q0=makeQuery(id+"F41.boolean.opBoolean","MERGE",FACE,{"derivedFrom":[makeQuery(id+"F39.boolean.opBoolean","MERGE",FACE,{"derivedFrom":[makeQuery(id+"F11.boolean.opBoolean","SPLIT",FACE,{"disambiguationData":[TD([makeQuery(id+"F11.opExtrude","SWEPT_FACE",FACE,{"disambiguationData":[OSD([sQuery(id+"F10.wireOp",EDGE,"E7.right")])]})])],"derivedFrom":makeQuery(id+"F9.boolean.opBoolean","COPY",FACE,{"derivedFrom":makeQuery(id+"F9.opExtrude","CAP_FACE",FACE,{"disambiguationData":[OSD([subQ0])],"isStart":false})})}),makeQuery(id+"F39.opExtrude","CAP_FACE",FACE,{"disambiguationData":[OSD([sQuery(id+"F38.wireOp",EDGE,"E32"),sQuery(id+"F38.wireOp",EDGE,"E33"),sQuery(id+"F38.wireOp",EDGE,"E34")])],"isStart":false})]}),makeQuery(id+"F41.opExtrude","CAP_FACE",FACE,{"disambiguationData":[OSD([sQuery(id+"F40.wireOp",EDGE,"E47"),sQuery(id+"F40.wireOp",EDGE,"E48"),sQuery(id+"F40.wireOp",EDGE,"E49"),sQuery(id+"F40.wireOp",EDGE,"E50")])],"isStart":false})]});}
            var sketch = newSketch(context, id + "F43", { "sketchPlane" : qUnion([Q0])});
            skLineSegment(sketch, "E57.bottom", {"start": v(15.8, -0.85) * mm, "end": v(18.8, -0.85) * mm});
            skLineSegment(sketch, "E57.top", {"start": v(15.8, -8.15) * mm, "end": v(18.8, -8.15) * mm});
            skLineSegment(sketch, "E57.left", {"start": v(15.8, -0.85) * mm, "end": v(15.8, -8.15) * mm});
            skLineSegment(sketch, "E57.right", {"start": v(18.8, -0.85) * mm, "end": v(18.8, -8.15) * mm});
            skLineSegment(sketch, "E58.2.0", {"start": v(-15.8, 0.85) * mm, "end": v(-18.8, 0.85) * mm});
            skLineSegment(sketch, "E58.2.1", {"start": v(-18.8, 0.85) * mm, "end": v(-18.8, 8.15) * mm});
            skLineSegment(sketch, "E58.2.2", {"start": v(-15.8, 8.15) * mm, "end": v(-18.8, 8.15) * mm});
            skLineSegment(sketch, "E58.2.3", {"start": v(-15.8, 0.85) * mm, "end": v(-15.8, 8.15) * mm});
            skPoint(sketch, "E58.center", {"position": v(0, 0) * mm});
            skLineSegment(sketch, "E58.anchor1", {"start": v(0, 0) * mm, "end": v(15.8, -0.85) * mm, "construction": true});
            skLineSegment(sketch, "E58.anchor2", {"start": v(0, 0) * mm, "end": v(-15.8, 0.85) * mm, "construction": true});
            skSolve(sketch);
        }
        {
            var Q0;
            Q0 = qSketchRegion(id + "F43", true);
            extrude(context, id + "F44", {"entities" : qUnion([Q0]), "operationType" : NewBodyOperationType.REMOVE, "oppositeDirection" : true, "depth" : 9 * mm, "offsetDistance" : 25 * mm});
        }
    });
